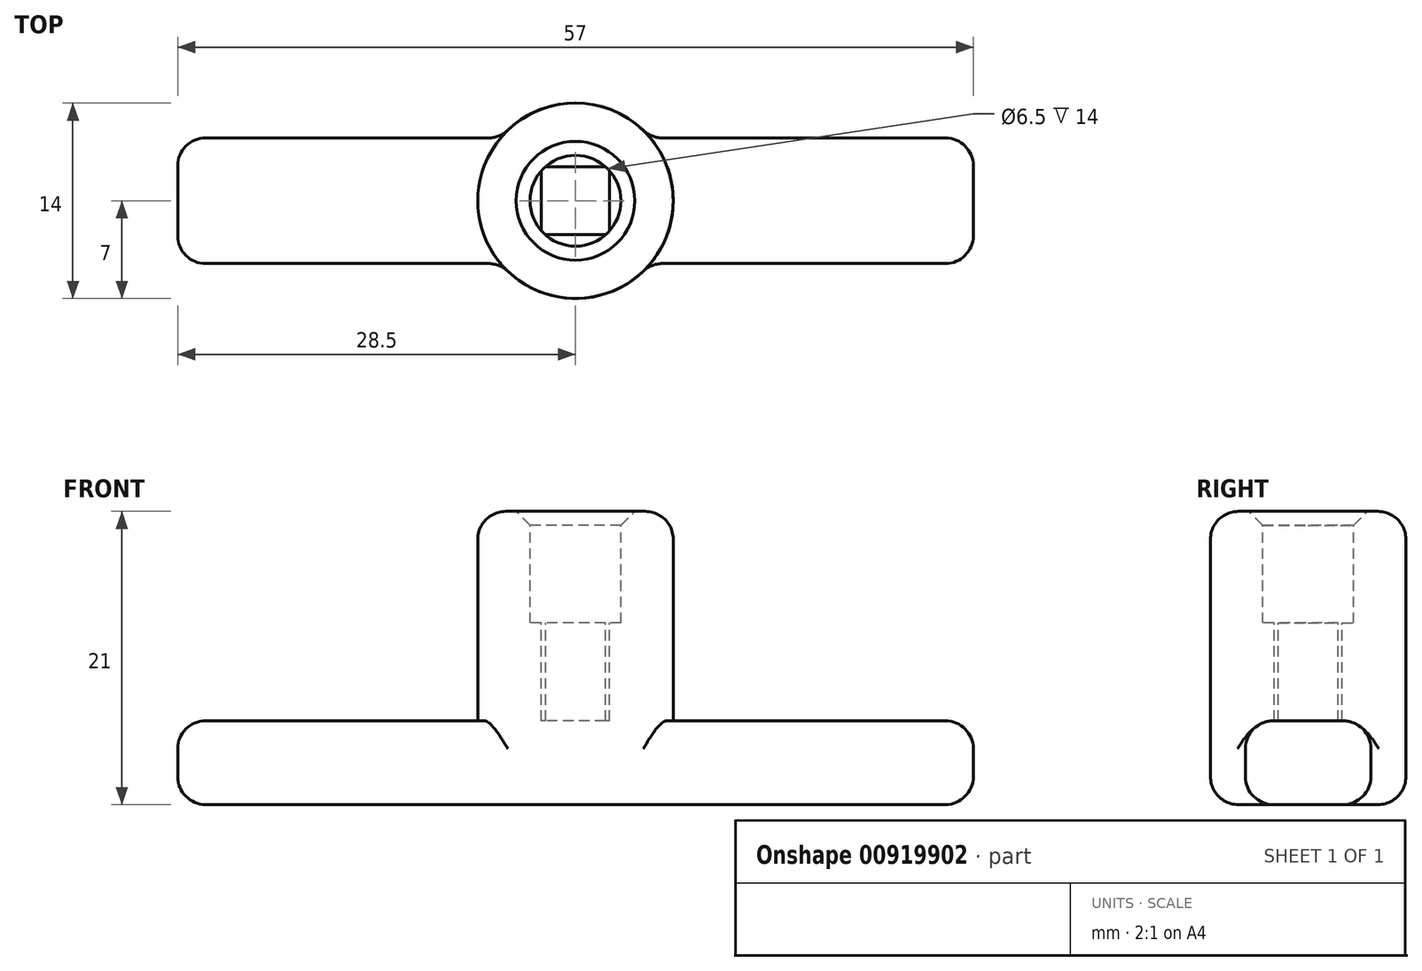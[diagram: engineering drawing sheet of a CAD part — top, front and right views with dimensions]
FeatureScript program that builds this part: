
annotation { "Feature Type Name" : "Feature", "Feature Type Description" : "" }
export const myFeature = defineFeature(function(context is Context, id is Id, definition is map)
    precondition{}
    {
        {
            var Q0;
            Q0=qCreatedBy(makeId("Top.planeOp"),FACE);
            var sketch = newSketch(context, id + "F0", { "sketchPlane" : qUnion([Q0])});
            skLineSegment(sketch, "E0.bottom", {"start": v(2.44, 2.44) * mm, "end": v(-2.44, 2.44) * mm});
            skLineSegment(sketch, "E0.top", {"start": v(2.44, -2.44) * mm, "end": v(-2.44, -2.44) * mm});
            skLineSegment(sketch, "E0.left", {"start": v(2.44, 2.44) * mm, "end": v(2.44, -2.44) * mm});
            skLineSegment(sketch, "E0.right", {"start": v(-2.44, 2.44) * mm, "end": v(-2.44, -2.44) * mm});
            skPoint(sketch, "E0.middle", {"position": v(0, 0) * mm});
            skCircle(sketch, "E1", {"center": v(0, 0) * mm, "radius": 7 * mm});
            skLineSegment(sketch, "E2", {"start": v(2.44, -2.44) * mm, "end": v(4.95, -4.95) * mm, "construction": true});
            skSolve(sketch);
        }
        {
            var Q0;
            Q0 = qSketchRegion(id + "F0", true);
            extrude(context, id + "F1", {"entities" : qUnion([Q0]), "depth" : 13 * mm, "offsetDistance" : 25.4 * mm});
        }
        {
            var Q0;
            Q0=qCreatedBy(makeId("Top.planeOp"),FACE);
            var sketch = newSketch(context, id + "F2", { "sketchPlane" : qUnion([Q0])});
            skLineSegment(sketch, "E3.bottom", {"start": v(28.5, 4.5) * mm, "end": v(-28.5, 4.5) * mm});
            skLineSegment(sketch, "E3.top", {"start": v(28.5, -4.5) * mm, "end": v(-28.5, -4.5) * mm});
            skLineSegment(sketch, "E3.left", {"start": v(28.5, 4.5) * mm, "end": v(28.5, -4.5) * mm});
            skLineSegment(sketch, "E3.right", {"start": v(-28.5, 4.5) * mm, "end": v(-28.5, -4.5) * mm});
            skPoint(sketch, "E3.middle", {"position": v(0, 0) * mm});
            skSolve(sketch);
        }
        {
            var Q0;
            Q0 = qSketchRegion(id + "F2", true);
            extrude(context, id + "F3", {"entities" : qUnion([Q0]), "operationType" : NewBodyOperationType.ADD, "depth" : 6 * mm, "offsetDistance" : 25.4 * mm});
        }
        {
            var Q0;
            Q0=makeQuery(id+"F1.opExtrude","CAP_FACE",FACE,{"disambiguationData":[OSD([sQuery(id+"F0.wireOp",EDGE,"E0.bottom"),sQuery(id+"F0.wireOp",EDGE,"E0.top"),sQuery(id+"F0.wireOp",EDGE,"E0.left"),sQuery(id+"F0.wireOp",EDGE,"E0.right"),sQuery(id+"F0.wireOp",EDGE,"E1")])],"isStart":false});
            var sketch = newSketch(context, id + "F4", { "sketchPlane" : qUnion([Q0])});
            skArc(sketch, "E4", {"start": v(-2.15, 2.44) * mm, "mid": v(-2.3, 2.3) * mm, "end": v(-2.44, 2.15) * mm});
            skLineSegment(sketch, "E5.0", {"start": v(2.44, 2.44) * mm, "end": v(2.15, 2.44) * mm});
            skLineSegment(sketch, "E5.1", {"start": v(-2.44, 2.44) * mm, "end": v(-2.44, 2.15) * mm});
            skLineSegment(sketch, "E5.2", {"start": v(2.44, -2.44) * mm, "end": v(2.15, -2.44) * mm});
            skLineSegment(sketch, "E5.3", {"start": v(2.44, 2.44) * mm, "end": v(2.44, 2.15) * mm});
            skLineSegment(sketch, "E6.trimOffspring", {"start": v(-2.15, 2.44) * mm, "end": v(-2.44, 2.44) * mm});
            skArc(sketch, "E7.trimOffspring", {"start": v(-2.44, -2.15) * mm, "mid": v(-2.3, -2.3) * mm, "end": v(-2.15, -2.44) * mm});
            skLineSegment(sketch, "E8.trimOffspring", {"start": v(-2.44, -2.15) * mm, "end": v(-2.44, -2.44) * mm});
            skLineSegment(sketch, "E9.trimOffspring", {"start": v(2.44, -2.15) * mm, "end": v(2.44, -2.44) * mm});
            skArc(sketch, "E10.trimOffspring", {"start": v(2.44, 2.15) * mm, "mid": v(2.3, 2.3) * mm, "end": v(2.15, 2.44) * mm});
            skLineSegment(sketch, "E11.trimOffspring", {"start": v(-2.15, -2.44) * mm, "end": v(-2.44, -2.44) * mm});
            skArc(sketch, "E12.trimOffspring", {"start": v(2.15, -2.44) * mm, "mid": v(2.3, -2.3) * mm, "end": v(2.44, -2.15) * mm});
            skSolve(sketch);
        }
        {
            var Q0;
            Q0 = qSketchRegion(id + "F4", true);
            extrude(context, id + "F5", {"entities" : qUnion([Q0]), "operationType" : NewBodyOperationType.ADD, "endBound" : BoundingType.UP_TO_NEXT, "oppositeDirection" : true, "depth" : 25.4 * mm, "offsetDistance" : 25.4 * mm});
        }
        {
            var Q0;
            Q0=makeQuery(id+"F5.boolean.opBoolean","MERGE",FACE,{"derivedFrom":[makeQuery(id+"F1.opExtrude","CAP_FACE",FACE,{"disambiguationData":[OSD([sQuery(id+"F0.wireOp",EDGE,"E0.bottom"),sQuery(id+"F0.wireOp",EDGE,"E0.top"),sQuery(id+"F0.wireOp",EDGE,"E0.left"),sQuery(id+"F0.wireOp",EDGE,"E0.right"),sQuery(id+"F0.wireOp",EDGE,"E1")])],"isStart":false}),makeQuery(id+"F5.opExtrude","CAP_FACE",FACE,{"disambiguationData":[OSD([sQuery(id+"F4.wireOp",EDGE,"E4"),sQuery(id+"F4.wireOp",EDGE,"E5.1"),sQuery(id+"F4.wireOp",EDGE,"E6.trimOffspring")])],"isStart":true}),makeQuery(id+"F5.opExtrude","CAP_FACE",FACE,{"disambiguationData":[OSD([sQuery(id+"F4.wireOp",EDGE,"E5.0"),sQuery(id+"F4.wireOp",EDGE,"E5.3"),sQuery(id+"F4.wireOp",EDGE,"E10.trimOffspring")])],"isStart":true}),makeQuery(id+"F5.opExtrude","CAP_FACE",FACE,{"disambiguationData":[OSD([sQuery(id+"F4.wireOp",EDGE,"E5.2"),sQuery(id+"F4.wireOp",EDGE,"E9.trimOffspring"),sQuery(id+"F4.wireOp",EDGE,"E12.trimOffspring")])],"isStart":true}),makeQuery(id+"F5.opExtrude","CAP_FACE",FACE,{"disambiguationData":[OSD([sQuery(id+"F4.wireOp",EDGE,"E7.trimOffspring"),sQuery(id+"F4.wireOp",EDGE,"E8.trimOffspring"),sQuery(id+"F4.wireOp",EDGE,"E11.trimOffspring")])],"isStart":true})]});
            var sketch = newSketch(context, id + "F6", { "sketchPlane" : qUnion([Q0])});
            skCircle(sketch, "E13.0", {"center": v(0, 0) * mm, "radius": 7 * mm});
            skCircle(sketch, "E14", {"center": v(0, 0) * mm, "radius": 3.25 * mm});
            skSolve(sketch);
        }
        {
            var Q0;
            Q0 = qSketchRegion(id + "F6", true);
            extrude(context, id + "F7", {"entities" : qUnion([Q0]), "operationType" : NewBodyOperationType.ADD, "depth" : 8 * mm, "offsetDistance" : 25.4 * mm});
        }
        {
            var Q0;
            Q0=makeQuery(id+"F7.opExtrude","CAP_EDGE",EDGE,{"disambiguationData":[OSD([sQuery(id+"F6.wireOp",EDGE,"E14")])],"isStart":false});
            chamfer(context, id + "F8", {"entities" : qUnion([Q0]), "width" : 1 * mm, "tangentPropagation" : true});
        }
        {
            var Q0;
            Q0=makeQuery(id+"F3.opExtrude","SWEPT_EDGE",EDGE,{"disambiguationData":[OSD([sQuery(id+"F2.wireOp",EDGE,"E3.top"),sQuery(id+"F2.wireOp",EDGE,"E3.right")])]});
            var Q1;
            Q1=makeQuery(id+"F3.opExtrude","SWEPT_EDGE",EDGE,{"disambiguationData":[OSD([sQuery(id+"F2.wireOp",EDGE,"E3.top"),sQuery(id+"F2.wireOp",EDGE,"E3.left")])]});
            var Q2;
            Q2=makeQuery(id+"F3.opExtrude","SWEPT_EDGE",EDGE,{"disambiguationData":[OSD([sQuery(id+"F2.wireOp",EDGE,"E3.bottom"),sQuery(id+"F2.wireOp",EDGE,"E3.left")])]});
            var Q3;
            Q3=makeQuery(id+"F3.opExtrude","SWEPT_EDGE",EDGE,{"disambiguationData":[OSD([sQuery(id+"F2.wireOp",EDGE,"E3.bottom"),sQuery(id+"F2.wireOp",EDGE,"E3.right")])]});
            var Q4;
            Q4=makeQuery(id+"F3.boolean.opBoolean","INTERSECT",EDGE,{"disambiguationData":[OD(1.0)],"derivedFrom":[makeQuery(id+"F1.opExtrude","SWEPT_FACE",FACE,{"disambiguationData":[OSD([sQuery(id+"F0.wireOp",EDGE,"E1")])]}),makeQuery(id+"F3.opExtrude","SWEPT_FACE",FACE,{"disambiguationData":[OSD([sQuery(id+"F2.wireOp",EDGE,"E3.bottom")])]})]});
            var Q5;
            Q5=makeQuery(id+"F3.boolean.opBoolean","INTERSECT",EDGE,{"disambiguationData":[OD(0.0)],"derivedFrom":[makeQuery(id+"F1.opExtrude","SWEPT_FACE",FACE,{"disambiguationData":[OSD([sQuery(id+"F0.wireOp",EDGE,"E1")])]}),makeQuery(id+"F3.opExtrude","SWEPT_FACE",FACE,{"disambiguationData":[OSD([sQuery(id+"F2.wireOp",EDGE,"E3.bottom")])]})]});
            var Q6;
            Q6=makeQuery(id+"F3.boolean.opBoolean","INTERSECT",EDGE,{"disambiguationData":[OD(0.0)],"derivedFrom":[makeQuery(id+"F1.opExtrude","SWEPT_FACE",FACE,{"disambiguationData":[OSD([sQuery(id+"F0.wireOp",EDGE,"E1")])]}),makeQuery(id+"F3.opExtrude","SWEPT_FACE",FACE,{"disambiguationData":[OSD([sQuery(id+"F2.wireOp",EDGE,"E3.top")])]})]});
            var Q7;
            Q7=makeQuery(id+"F3.boolean.opBoolean","INTERSECT",EDGE,{"disambiguationData":[OD(1.0)],"derivedFrom":[makeQuery(id+"F1.opExtrude","SWEPT_FACE",FACE,{"disambiguationData":[OSD([sQuery(id+"F0.wireOp",EDGE,"E1")])]}),makeQuery(id+"F3.opExtrude","SWEPT_FACE",FACE,{"disambiguationData":[OSD([sQuery(id+"F2.wireOp",EDGE,"E3.top")])]})]});
            fillet(context, id + "F9", {"entities" : qUnion([Q0, Q1, Q2, Q3, Q4, Q5, Q6, Q7]), "radius" : 2 * mm, "tangentPropagation" : true, "allowEdgeOverflow" : false});
        }
        {
            var Q0;
            {var subQ0=sQuery(id+"F2.wireOp",EDGE,"E3.top");var subQ1=sQuery(id+"F2.wireOp",EDGE,"E3.right");Q0=makeQuery(id+"F3.boolean.opBoolean","SPLIT",EDGE,{"disambiguationData":[TD([makeQuery(id+"F3.opExtrude","SWEPT_FACE",FACE,{"disambiguationData":[OSD([subQ1])]})])],"derivedFrom":makeQuery(id+"F3.opExtrude","CAP_EDGE",EDGE,{"disambiguationData":[OSD([subQ0])],"isStart":false})});}
            var Q1;
            {var subQ0=sQuery(id+"F2.wireOp",EDGE,"E3.right");var subQ1=sQuery(id+"F2.wireOp",EDGE,"E3.top");Q1=makeQuery(id+"F3.boolean.opBoolean","SPLIT",EDGE,{"disambiguationData":[TD([makeQuery(id+"F3.opExtrude","SWEPT_FACE",FACE,{"disambiguationData":[OSD([subQ0])]})])],"derivedFrom":makeQuery(id+"F3.opExtrude","CAP_EDGE",EDGE,{"disambiguationData":[OSD([subQ1])],"isStart":true})});}
            var Q2;
            {var subQ0=sQuery(id+"F2.wireOp",EDGE,"E3.top");var subQ1=sQuery(id+"F2.wireOp",EDGE,"E3.left");Q2=makeQuery(id+"F3.boolean.opBoolean","SPLIT",EDGE,{"disambiguationData":[TD([makeQuery(id+"F3.opExtrude","SWEPT_FACE",FACE,{"disambiguationData":[OSD([subQ1])]})])],"derivedFrom":makeQuery(id+"F3.opExtrude","CAP_EDGE",EDGE,{"disambiguationData":[OSD([subQ0])],"isStart":false})});}
            var Q3;
            Q3=makeQuery(id+"F7.opExtrude","CAP_EDGE",EDGE,{"disambiguationData":[OSD([sQuery(id+"F6.wireOp",EDGE,"E13.0")])],"isStart":false});
            fillet(context, id + "F10", {"entities" : qUnion([Q0, Q1, Q2, Q3]), "radius" : 2 * mm, "tangentPropagation" : true, "allowEdgeOverflow" : false});
        }
    });
